# Revit family: EKF_EE_МонтажнаяПанельFORT_PROxima
name_source: partatom
category: Электрооборудование
units: mm (PartAtom-declared; Revit-internal decimal feet)

## family parameters
Всегда вертикально = Нет
На основе рабочей плоскости = Да
Общий = Да
При загрузке вырезать с полостями = Нет
Размер круглого соединителя = Использовать диаметр
Тип детали = Силовой щит
Точка расчета площади = Нет

## types (8) — shared parameters
ADSK_Единица измерения = шт.
ADSK_Завод-изготовитель = EKF
ADSK_Количество = 1
ADSK_Марка = Монтажная панель FORT
ADSK_Материал = RAL 7035_Сталь
ADSK_Обозначение = Монтажная панель FORT
ADSK_Размер_Глубина = 2 мм
Изготовитель = EKF
КолОтв = 2
Отступ = 20 мм
Серия номенклатуры = PROxima
Степень защиты IP = -
ТВ = EKF_2
Тип установки = -
zero-valued in all types: ADSK_Масса, Отметка по умолчанию

## per-type parameters (varying)
| type | ADSK_Код изделия | ADSK_Размер_Высота | ADSK_Размер_Ширина | D | Тип |
| Монтажная панель FORT (В300хШ1000) EKF PROxima | FM310 | 300 мм | 1000 мм | 10 мм | 250 мм |
| Монтажная панель FORT (В300хШ400) EKF PROxima | FM34 | 300 мм | 400 мм | 10 мм | 251 мм |
| Монтажная панель FORT (В300хШ600) EKF PROxima | FM36 | 300 мм | 600 мм | 10 мм | 252 мм |
| Монтажная панель FORT (В400хШ1000) EKF PROxima | FM410 | 400 мм | 1000 мм | 10 мм | 254 мм |
| Монтажная панель FORT (В400хШ400) EKF PROxima | FM44 | 400 мм | 400 мм | 10 мм | 255 мм |
| Монтажная панель FORT (В400хШ600) EKF PROxima | FM46 | 400 мм | 600 мм | 10 мм | 256 мм |
| Монтажная панель FORT (В400хШ800) EKF PROxima | FM48 | 400 мм | 800 мм | 10 мм | 257 мм |
| Монтажная панель FORT (В300хШ800) EKF PROxima | FM38 | 300 мм | 800 мм | 6.5 мм | 253 мм |

note: column(s) folded — value = type name in every type: ADSK_Наименование
